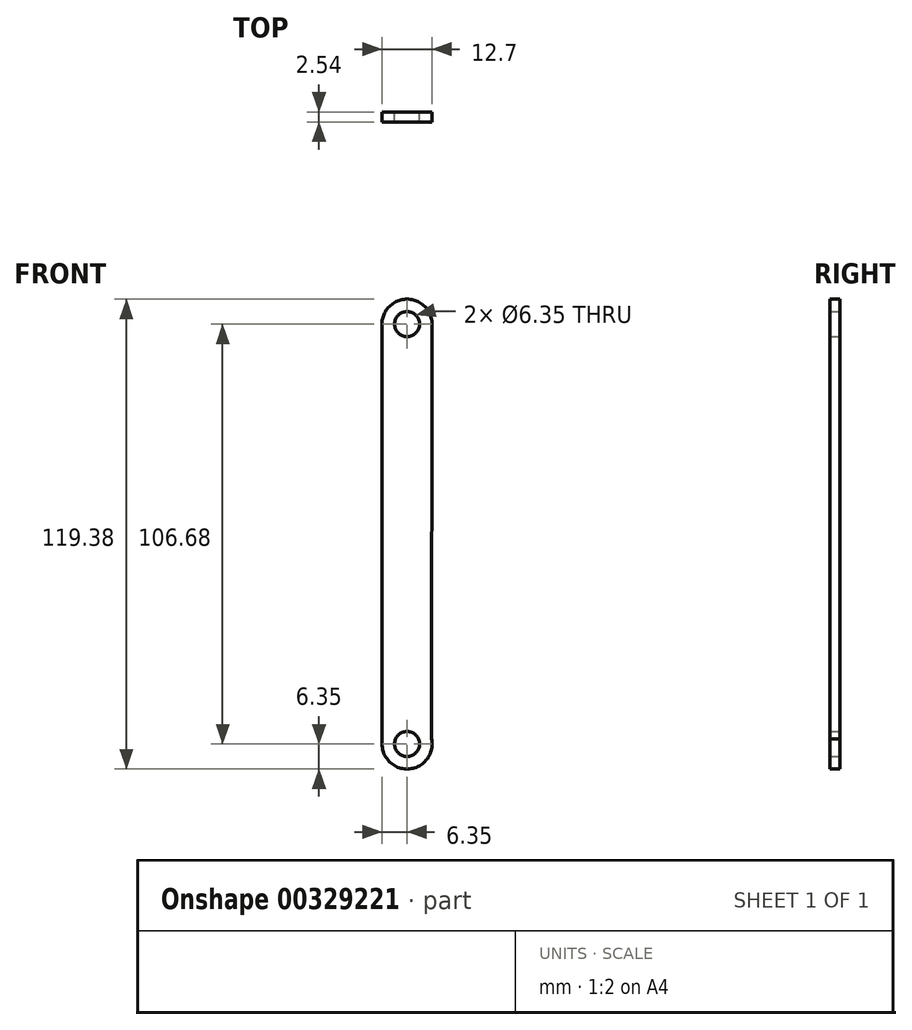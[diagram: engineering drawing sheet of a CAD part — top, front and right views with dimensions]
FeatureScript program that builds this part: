
annotation { "Feature Type Name" : "Feature", "Feature Type Description" : "" }
export const myFeature = defineFeature(function(context is Context, id is Id, definition is map)
    precondition{}
    {
        {
            var Q0;
            Q0=qCreatedBy(makeId("Front.planeOp"),FACE);
            var sketch = newSketch(context, id + "F0", { "sketchPlane" : qUnion([Q0])});
            skCircle(sketch, "E0", {"center": v(0, 0) * mm, "radius": 3.18 * mm});
            skCircle(sketch, "E1", {"center": v(0, 106.68) * mm, "radius": 6.35 * mm});
            skCircle(sketch, "E2", {"center": v(0, 106.68) * mm, "radius": 3.18 * mm});
            skCircle(sketch, "E3", {"center": v(0, 0) * mm, "radius": 6.35 * mm});
            skLineSegment(sketch, "E4", {"start": v(-6.35, 106.68) * mm, "end": v(-6.35, 0) * mm});
            skLineSegment(sketch, "E5", {"start": v(6.35, 106.67) * mm, "end": v(6.22, 1.3) * mm});
            skSolve(sketch);
        }
        {
            var Q0;
            Q0=makeQuery(id+"F0.imprint","IMPRINT",FACE,{"disambiguationData":[TD([[makeQuery(id+"F0.imprint","IMPRINT",EDGE,{"derivedFrom":sQuery(id+"F0.wireOp",EDGE,"E0")}),-1.0]])]});
            var Q1;
            {var subQ0=sQuery(id+"F0.wireOp",EDGE,"E4");Q1=makeQuery(id+"F0.imprint","IMPRINT",FACE,{"disambiguationData":[TD([[makeQuery(id+"F0.imprint","IMPRINT",EDGE,{"derivedFrom":subQ0}),1.0]])]});}
            var Q2;
            Q2=makeQuery(id+"F0.imprint","IMPRINT",FACE,{"disambiguationData":[TD([[makeQuery(id+"F0.imprint","IMPRINT",EDGE,{"derivedFrom":sQuery(id+"F0.wireOp",EDGE,"E2")}),-1.0]])]});
            extrude(context, id + "F1", {"entities" : qUnion([Q0, Q1, Q2]), "depth" : 2.54 * mm});
        }
    });
